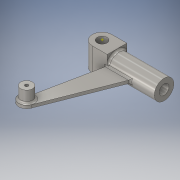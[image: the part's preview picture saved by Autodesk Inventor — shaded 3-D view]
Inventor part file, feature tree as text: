
AUTODESK INVENTOR PART (.ipt)
format: ipt  version: 2016 (Build 200138000, 138)  size: 208,384 bytes
history: native  units: in
note: dims shown in document units (in); Inventor stores cm internally (conversion verified against a paired STEP export)
features: other x9, sketch x5
ambient origin geometry x8: Origin, YZ Plane, XZ Plane, XY Plane, X Axis, Y Axis, Z Axis, Center Point
bodies: Solid1 (feature_tree)
feature tree (14):
  other  "Tie Rod to Front Axle Connecting Plate.ipt"
  other  "Solid1::Tie Rod to Front Axle Connecting Plate.ipt"
  other  "TaggingFeature1"
  sketch  "Sketch1"  dims[d0=0.3937in]
  sketch  "Sketch5"
  sketch  "Sketch6"
  sketch  "Sketch7"
  sketch  "Sketch9"
  other  "Main Plate Midplane"
  other  "Axle Hole Plane"
  other  "Main Plate Midplane1"
  other  "Axle Centerline"
  other  "Rotational Hole Axis"
  other  "Work Point1"
